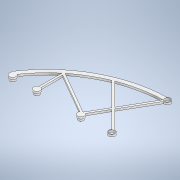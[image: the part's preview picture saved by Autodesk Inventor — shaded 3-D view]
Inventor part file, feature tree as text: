
AUTODESK INVENTOR PART (.ipt)
format: ipt  version: 2022.1 (Build 261234000, 234)  size: 227,328 bytes
history: native  units: in
note: dims shown in document units (in); Inventor stores cm internally (conversion verified against a paired STEP export)
features: extrude x5, sketch x4, fillet x2
ambient origin geometry x8: Origin, YZ Plane, XZ Plane, XY Plane, X Axis, Y Axis, Z Axis, Center Point
bodies: Solid1 (feature_tree)
feature tree (11):
  extrude  "Extrusion1"  Depth=5.9843in
  extrude  "Extrusion2"  TaperAngle=0.0deg  [1 undecoded]
  extrude  "Circular_Mounts"  Depth=0.125in
  sketch  "Sketch4"  dims[d9=0.125in d10=0.25in d11=0.25in d12=0.1387in d13=0.1387in d14=0.1181in d15=0.0in d16=7.874in d17=7.874in d18=0.125in d19=0.0in d20=0.3937in d21=0.1181in d22=0.0in d23=0.3189in d24=0.2756in d25=0.0in d27=0.0197in d28=0.0787in d29=0.1181in d30=6.1923in d31=0.0in d32=0.0in]
  extrude  "Inserts"  Depth=0.1181in
  fillet  "Fillet2"  Radius=0.25in
  fillet  "Fillet3"  Radius=0.1387in
  extrude  "Extrusion5"  Depth=0.1181in
  sketch  "Sketch1"  dims[d0=5.9843in d1=5.9843in]
  sketch  "Sketch2"  dims[d2=3.937in d3=0.0in]
  sketch  "Sketch3"  dims[d4=45.0deg d8=0.125in]
note: 1 required parameter value undecoded (feature->parameter linkage not recoverable at this tier; creation-order binding heuristic only, values carry confidence <= 0.55)
